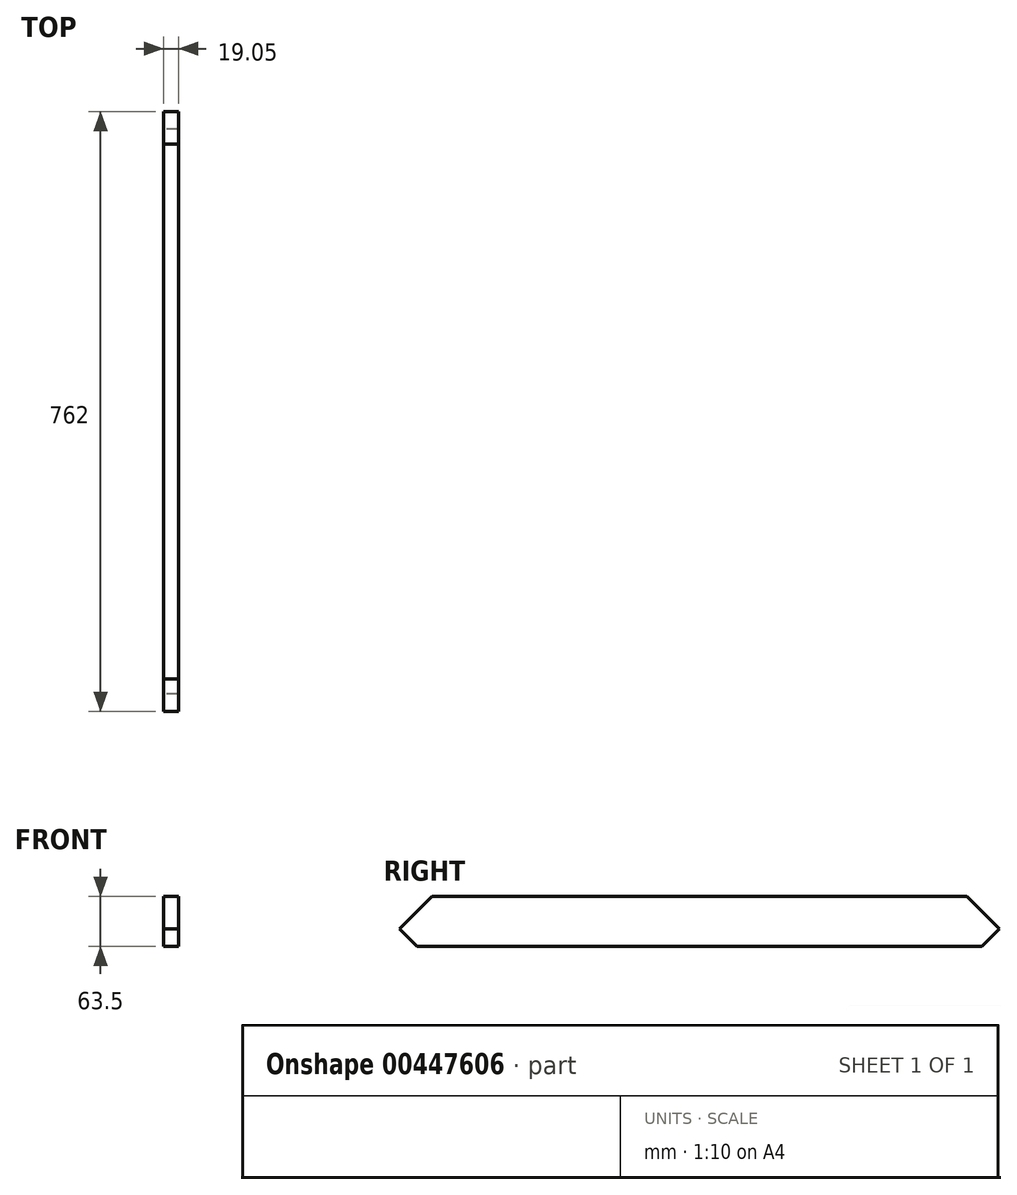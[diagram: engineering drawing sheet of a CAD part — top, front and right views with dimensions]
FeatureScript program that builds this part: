
annotation { "Feature Type Name" : "Feature", "Feature Type Description" : "" }
export const myFeature = defineFeature(function(context is Context, id is Id, definition is map)
    precondition{}
    {
        {
            var Q0;
            Q0=qCreatedBy(makeId("Front.planeOp"),FACE);
            var sketch = newSketch(context, id + "F0", { "sketchPlane" : qUnion([Q0])});
            skLineSegment(sketch, "E0.bottom", {"start": v(0, 0) * mm, "end": v(19.05, 0) * mm});
            skLineSegment(sketch, "E0.top", {"start": v(0, -63.5) * mm, "end": v(19.05, -63.5) * mm});
            skLineSegment(sketch, "E0.left", {"start": v(0, 0) * mm, "end": v(0, -63.5) * mm});
            skLineSegment(sketch, "E0.right", {"start": v(19.05, 0) * mm, "end": v(19.05, -63.5) * mm});
            skSolve(sketch);
        }
        {
            var Q0;
            Q0 = qSketchRegion(id + "F0", true);
            extrude(context, id + "F1", {"entities" : qUnion([Q0]), "depth" : 762 * mm, "offsetDistance" : 25.4 * mm});
        }
        {
            var Q0;
            Q0=makeQuery(id+"F1.opExtrude","CAP_EDGE",EDGE,{"disambiguationData":[OSD([sQuery(id+"F0.wireOp",EDGE,"E0.bottom")])],"isStart":true});
            var Q1;
            Q1=makeQuery(id+"F1.opExtrude","CAP_EDGE",EDGE,{"disambiguationData":[OSD([sQuery(id+"F0.wireOp",EDGE,"E0.bottom")])],"isStart":false});
            chamfer(context, id + "F2", {"entities" : qUnion([Q0, Q1]), "width" : 41.05 * mm, "tangentPropagation" : true});
        }
        {
            var Q0;
            {var subQ0=sQuery(id+"F0.wireOp",EDGE,"E0.bottom");Q0=makeQuery(id+"F2.opChamfer","BLEND_FACE",FACE,{"disambiguationData":[OSD([subQ0]),TDD([makeQuery(id+"F1.opExtrude","CAP_EDGE",EDGE,{"disambiguationData":[OSD([subQ0])],"isStart":true})])]});}
            var sketch = newSketch(context, id + "F3", { "sketchPlane" : qUnion([Q0])});
            skCircle(sketch, "E1", {"center": v(9.53, 0) * mm, "radius": 1.59 * mm});
            skLineSegment(sketch, "E2", {"start": v(19.05, 0) * mm, "end": v(0, 0) * mm, "construction": true});
            skPoint(sketch, "E2.endSnap0", {"position": v(19.05, 0) * mm});
            skSolve(sketch);
        }
        {
            var Q0;
            {var subQ0=sQuery(id+"F0.wireOp",EDGE,"E0.bottom");Q0=makeQuery(id+"F2.opChamfer","BLEND_FACE",FACE,{"disambiguationData":[OSD([subQ0]),TDD([makeQuery(id+"F1.opExtrude","CAP_EDGE",EDGE,{"disambiguationData":[OSD([subQ0])],"isStart":true})])]});}
            cPlane(context, id + "F4", {"entities" : qUnion([Q0]), "cplaneType" : CPlaneType.OFFSET, "offset" : 63.5 * mm, "oppositeDirection" : true, "width" : 152.4 * mm, "height" : 152.4 * mm});
        }
        {
            var Q0;
            Q0=qCreatedBy(id+"F4.planeOp",FACE);
            var sketch = newSketch(context, id + "F5", { "sketchPlane" : qUnion([Q0])});
            skCircle(sketch, "E3.0", {"center": v(-9.53, 0) * mm, "radius": 3.18 * mm, "construction": true});
            skCircle(sketch, "E4", {"center": v(-9.53, 0) * mm, "radius": 4.76 * mm});
            skSolve(sketch);
        }
        {
            var Q0;
            Q0=makeQuery(id+"F1.opExtrude","SWEPT_FACE",FACE,{"disambiguationData":[OSD([sQuery(id+"F0.wireOp",EDGE,"E0.left")])]});
            var sketch = newSketch(context, id + "F6", { "sketchPlane" : qUnion([Q0])});
            skLineSegment(sketch, "E5", {"start": v(0, -63.5) * mm, "end": v(0, -41.05) * mm});
            skLineSegment(sketch, "E6", {"start": v(0, -41.05) * mm, "end": v(22.45, -63.5) * mm});
            skLineSegment(sketch, "E7", {"start": v(22.45, -63.5) * mm, "end": v(0, -63.5) * mm});
            skSolve(sketch);
        }
        {
            var Q0;
            Q0 = qSketchRegion(id + "F6", true);
            extrude(context, id + "F7", {"entities" : qUnion([Q0]), "operationType" : NewBodyOperationType.REMOVE, "endBound" : BoundingType.THROUGH_ALL, "oppositeDirection" : true, "depth" : 25.4 * mm, "offsetDistance" : 25.4 * mm});
        }
        {
            var Q0;
            Q0=makeQuery(id+"F1.opExtrude","CAP_EDGE",EDGE,{"disambiguationData":[OSD([sQuery(id+"F0.wireOp",EDGE,"E0.top")])],"isStart":false});
            chamfer(context, id + "F8", {"entities" : qUnion([Q0]), "width" : 22.45 * mm, "tangentPropagation" : true});
        }
    });
